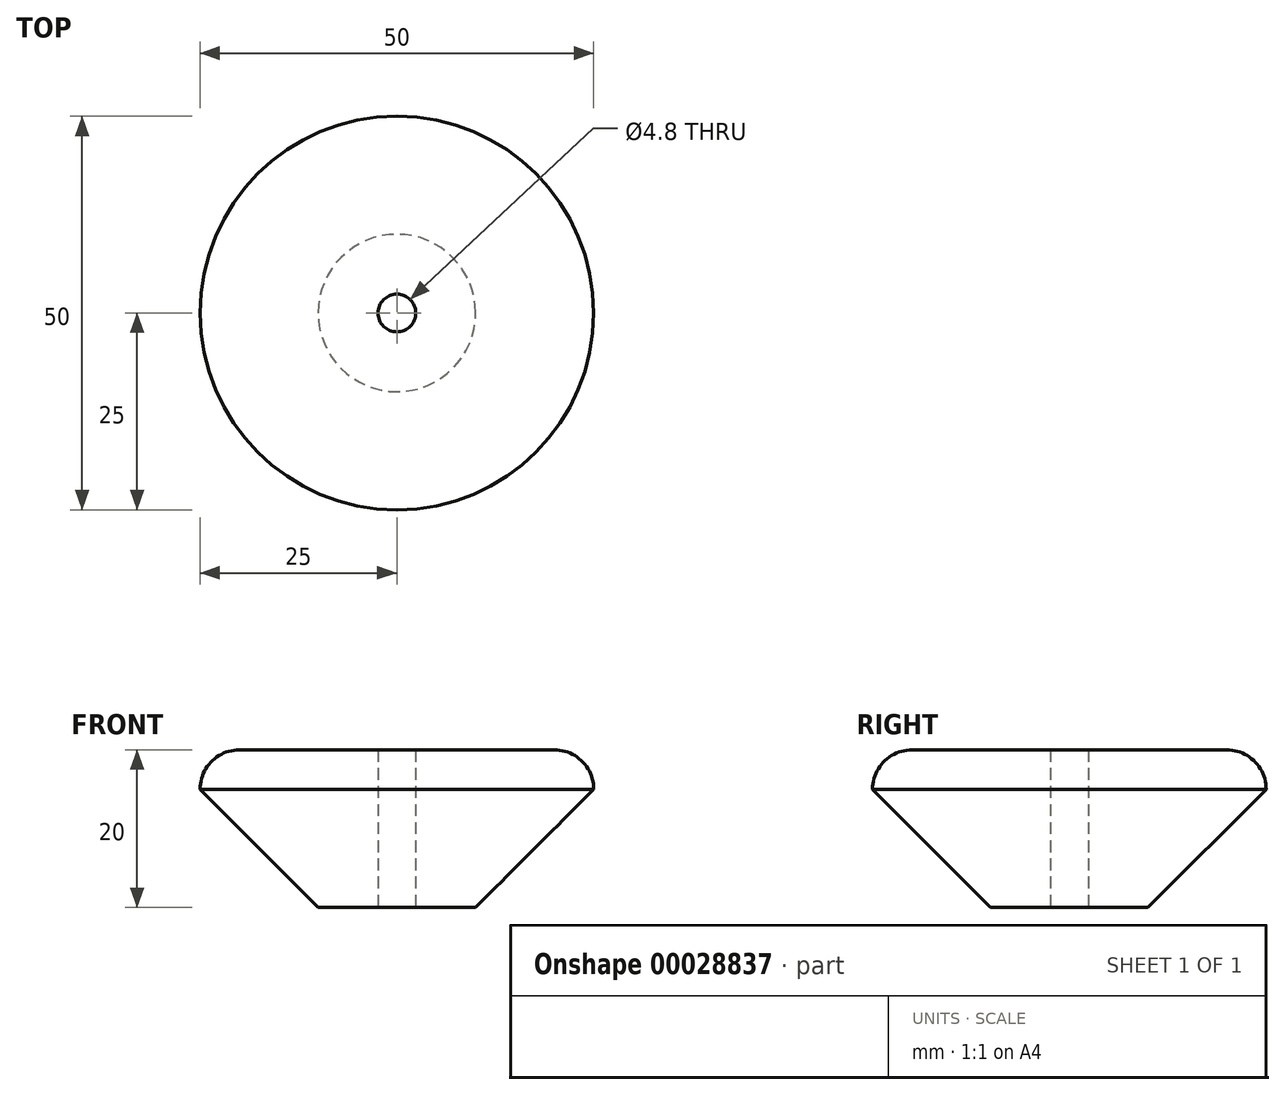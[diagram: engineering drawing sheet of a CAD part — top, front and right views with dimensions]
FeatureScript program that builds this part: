
annotation { "Feature Type Name" : "Feature", "Feature Type Description" : "" }
export const myFeature = defineFeature(function(context is Context, id is Id, definition is map)
    precondition{}
    {
        {
            var Q0;
            Q0=qCreatedBy(makeId("Top.planeOp"),FACE);
            var sketch = newSketch(context, id + "F0", { "sketchPlane" : qUnion([Q0])});
            skCircle(sketch, "E0", {"center": v(0, 0) * mm, "radius": 25 * mm});
            skCircle(sketch, "E1", {"center": v(0, 0) * mm, "radius": 2.4 * mm});
            skSolve(sketch);
        }
        {
            var Q0;
            Q0 = qSketchRegion(id + "F0", true);
            var Q1;
            Q1=makeQuery(id+"F0.imprint","IMPRINT",FACE,{"disambiguationData":[TD([[makeQuery(id+"F0.imprint","IMPRINT",EDGE,{"derivedFrom":sQuery(id+"F0.wireOp",EDGE,"E0")}),1.0]])]});
            extrude(context, id + "F1", {"entities" : qUnion([Q0, Q1]), "depth" : 20 * mm});
        }
        {
            var Q0;
            Q0=makeQuery(id+"F1.opExtrude","CAP_EDGE",EDGE,{"disambiguationData":[OSD([sQuery(id+"F0.wireOp",EDGE,"E0")])],"isStart":true});
            chamfer(context, id + "F2", {"entities" : qUnion([Q0]), "width" : 15 * mm, "tangentPropagation" : true});
        }
        {
            var Q0;
            Q0=makeQuery(id+"F1.opExtrude","CAP_EDGE",EDGE,{"disambiguationData":[OSD([sQuery(id+"F0.wireOp",EDGE,"E0")])],"isStart":false});
            fillet(context, id + "F3", {"entities" : qUnion([Q0]), "radius" : 5 * mm, "tangentPropagation" : true, "allowEdgeOverflow" : false});
        }
    });
